# Revit family: 46132009(2023)
name_source: partatom
category: Plumbing Fixtures
units: mm (PartAtom-declared; Revit-internal decimal feet)

## family parameters
Always vertical = Yes
Cut with Voids When Loaded = No
OmniClass Number = 23.45.55.00
OmniClass Title = Sanitary Faucets, Wastes
Part Type = Normal
Room Calculation Point = No
Round Connector Dimension = Use Diameter
Shared = No
Work Plane-Based = No

## types (1)
- 46132009 Kitchen faucet, 230/9 V, Bluetooth
    2D/3D/BIM Files URL = http://static.hansa.com
    3D View = https://static.hansa.com
    Advanced Features = Inner body made of DZR brass;3S-installation system for safe and simple mounting
    Aerator = Laminar stream
    AssetType = Fixed
    Automatic Flush Frequency = off (off/1-120 h)
    Automatic Flush Period = 30 s (1-1800 s)
    BIMObjectName = 46132009(2023)
    Backflow Prevention EN1717 = AA
    Bluetooth = 5.x (D060576)
    BodyMaterial = Brass
    Brand = HANSA
    Catalog Drawing URL = http://static.hansa.com
    CloseOffRating = 0
    Color = Chrome
    Connection = Flexible inlet pipes
    Connection Size = G3/8
    Default Elevation = 0 mm  [stored 0 ft]
    Dimension Drawing URL = http://static.hansa.com
    DurationUnit = Year
    EAN Number = 4057304019661
    EMC Directive = 2014/53/EU , 2011/65/EU
    EN Standard = EN 817, EN 15091
    ETIM Class Number = EC011431 Kitchen mixing tap
    Electrical Connection = 230 / 9 V
    Electronic Parts = ;Solenoid valve;Power supply
    FDV Document URL = http://www.hansa.com
    FaucetMainMaterial = Brass
    Features = Hybrid;Bluetooth®
    Finish = Polished
    Flow Drawing URL = http://static.hansa.com
    Flow Rate At 300kPa = 0.0 L/s
    FlowCoefficient = 0
    Group = Kitchen faucet
    IfcExportAs = IfcValveType
    IfcExportType = FAUCET
    InletConnectionSize = 10 mm  [stored 0.0328084 ft]
    Installation Type = Deck mounted
    Installation and Maintenance Guide URL = http://static.hansa.com
    Interactive AR View URL = https://static.hansa.com
    Lever Handle = Single operating lever/handle;Hot/Cold symbols
    Long Marketing = Care  Hybrid series is giving you a whole new modern design to fit into any kitchen. Lever can easily be moved by using the backside of the hand and with our intelligent touchless functions build into same faucet it also supports hygiene operation without any touch needed.
    Manufacturer = HANSA
    ManufacturerName = HANSA
    ManufacturerURL = http://www.hansa.com
    Market = International;Germany;Austria;Switzerland;Belgium;Netherlands;Italy
    Material = Brass
    Max Flow Period = 10 s(1 - 1800 s)
    Max. Hot Water Supply = 70 °C
    Mechanical Parts = ø 40 mm ceramic cartridge for flow and temperature control
    Mobile Product Information URL = http://mpi.hansa.com
    Model = 46132009 Kitchen faucet, 230/9 V, Bluetooth
    ModelReference = 46132009
    Mounting Holes = 1 hole
    NBSDescription = Water supply fittings for wash basins and troughs
    NBSReference = 45-35-70/371
    Name = 46132009 Kitchen faucet, 230/9 V, Bluetooth
    Name_en = 46132009 Kitchen faucet, 230/9 V, Bluetooth
    Noise Class = I (ISO 3822)
    NominalDepth = 254 mm
    NominalHeight = 183 mm
    NominalWidth = 54 mm
    Operating Voltage = 9 V
    Pressure Loss With Flow 02ls = 195000.0 Pa
    Product Code = 46132009
    Product Family = HANSACARE Hybrid
    Product Image URL = http://static.hansa.com
    Product URL = http://static.hansa.com
    Protection Class = IP 55 / transformer IP 20
    Shape = Sculptured
    Size = 55x255x185 mm
    Spout Projection = 214 mm
    Spout Swivel Range = 120° (80°/40°)
    Spout Type = Swivel spout;Swivel range limiting option;Profile construction
    Surface treatment = Chrome
    Technical DataSheet URL = http://www.hansa.com
    Temperature Adjustments = Limitation option for maximum temperature and flow-rate
    UNSPSC Class Number = 30181700 Faucets or taps
    URL Declaration Of Performance (DOP) = http://static.hansa.com
    URL Declaration of Asbestos = http://static.hansa.com
    URL Declaration of Conformity = http://static.hansa.com
    URL Declaration of SCIP = http://static.hansa.com
    URL EU Packaging Declaration = http://static.hansa.com
    URL EcoLabel Declaration = http://static.hansa.com
    URL REACH = http://static.hansa.com
    URL UWL = http://static.hansa.com
    URL WEEE = http://static.hansa.com
    Uniclass2 = Pr_40_30_96_96
    Uniclass2015Description = Washbasin manual water supply sets
    Uniclass2015Reference = Pr_40_20_87_96
    Version = 1
    VersionDate = 01/06/2023
    Warranty Information URL = http://warranty.hansa.com
    WarrantyDescription = http://warranty.hansa.com
    WarrantyDurationUnit = Year
    Working Pressure = 50 - 1000 kPa

note: [stored X ft] marks values corroborated as IEEE doubles in the binary element streams (Revit-internal decimal feet)

## geometry (parser evidence)
native form markers: Sweep x6
no freeform markers — native parametric forms only
